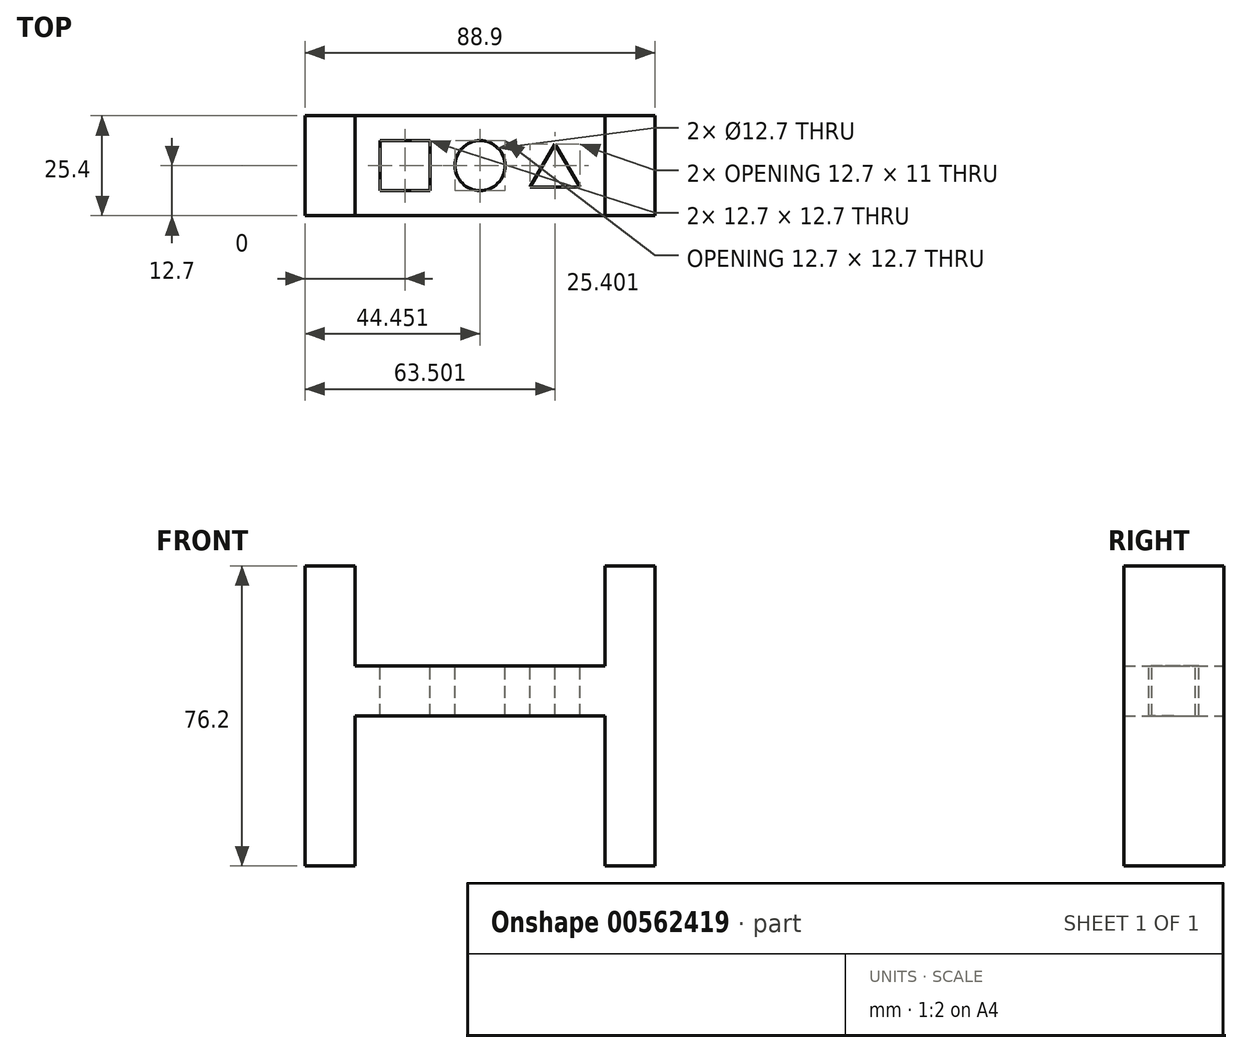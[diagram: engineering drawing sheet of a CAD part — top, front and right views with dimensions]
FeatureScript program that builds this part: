
annotation { "Feature Type Name" : "Feature", "Feature Type Description" : "" }
export const myFeature = defineFeature(function(context is Context, id is Id, definition is map)
    precondition{}
    {
        {
            var Q0;
            Q0=qCreatedBy(makeId("Front.planeOp"),FACE);
            var sketch = newSketch(context, id + "F0", { "sketchPlane" : qUnion([Q0])});
            skLineSegment(sketch, "E0", {"start": v(-59.33, 38.1) * mm, "end": v(-46.63, 38.1) * mm});
            skLineSegment(sketch, "E1", {"start": v(-46.63, 38.1) * mm, "end": v(-46.63, 12.7) * mm});
            skLineSegment(sketch, "E2", {"start": v(-46.63, 12.7) * mm, "end": v(16.87, 12.7) * mm});
            skLineSegment(sketch, "E3", {"start": v(16.87, 12.7) * mm, "end": v(16.87, 38.1) * mm});
            skLineSegment(sketch, "E4", {"start": v(16.87, 38.1) * mm, "end": v(29.57, 38.1) * mm});
            skLineSegment(sketch, "E5", {"start": v(29.57, 38.1) * mm, "end": v(29.57, -38.1) * mm});
            skLineSegment(sketch, "E6", {"start": v(29.57, -38.1) * mm, "end": v(16.87, -38.1) * mm});
            skLineSegment(sketch, "E7", {"start": v(16.87, -38.1) * mm, "end": v(16.87, 0) * mm});
            skLineSegment(sketch, "E8", {"start": v(16.87, 0) * mm, "end": v(-46.63, 0) * mm});
            skLineSegment(sketch, "E9", {"start": v(-46.63, 0) * mm, "end": v(-46.63, -38.1) * mm});
            skLineSegment(sketch, "E10", {"start": v(-46.63, -38.1) * mm, "end": v(-59.33, -38.1) * mm});
            skLineSegment(sketch, "E11", {"start": v(-59.33, -38.1) * mm, "end": v(-59.33, 38.1) * mm});
            skSolve(sketch);
        }
        {
            var Q0;
            Q0=makeQuery(id+"F0.imprint","IMPRINT",FACE,{"disambiguationData":[TD([[makeQuery(id+"F0.imprint","IMPRINT",EDGE,{"derivedFrom":sQuery(id+"F0.wireOp",EDGE,"E0")}),-1.0]])]});
            extrude(context, id + "F1", {"entities" : qUnion([Q0]), "depth" : 25.4 * mm, "offsetDistance" : 25.4 * mm});
        }
        {
            var Q0;
            Q0=makeQuery(id+"F1.opExtrude","SWEPT_FACE",FACE,{"disambiguationData":[OSD([sQuery(id+"F0.wireOp",EDGE,"E2")])]});
            var sketch = newSketch(context, id + "F2", { "sketchPlane" : qUnion([Q0])});
            skLineSegment(sketch, "E12.bottom", {"start": v(-40.28, -6.35) * mm, "end": v(-27.58, -6.35) * mm});
            skLineSegment(sketch, "E12.top", {"start": v(-40.28, -19.05) * mm, "end": v(-27.58, -19.05) * mm});
            skLineSegment(sketch, "E12.left", {"start": v(-40.28, -6.35) * mm, "end": v(-40.28, -19.05) * mm});
            skLineSegment(sketch, "E12.right", {"start": v(-27.58, -6.35) * mm, "end": v(-27.58, -19.05) * mm});
            skSolve(sketch);
        }
        {
            var Q0;
            Q0=makeQuery(id+"F2.imprint","IMPRINT",FACE,{"disambiguationData":[TD([[makeQuery(id+"F2.imprint","IMPRINT",EDGE,{"derivedFrom":sQuery(id+"F2.wireOp",EDGE,"E12.bottom")}),-1.0]])]});
            extrude(context, id + "F3", {"entities" : qUnion([Q0]), "operationType" : NewBodyOperationType.REMOVE, "oppositeDirection" : true, "depth" : 25.4 * mm, "offsetDistance" : 25.4 * mm});
        }
        {
            var Q0;
            Q0=makeQuery(id+"F1.opExtrude","SWEPT_FACE",FACE,{"disambiguationData":[OSD([sQuery(id+"F0.wireOp",EDGE,"E2")])]});
            var sketch = newSketch(context, id + "F4", { "sketchPlane" : qUnion([Q0])});
            skCircle(sketch, "E13", {"center": v(-14.88, -12.7) * mm, "radius": 6.35 * mm});
            skPoint(sketch, "E13.centerSnap0", {"position": v(-27.58, -12.7) * mm});
            skSolve(sketch);
        }
        {
            var Q0;
            Q0=makeQuery(id+"F4.imprint","IMPRINT",FACE,{"disambiguationData":[TD([[makeQuery(id+"F4.imprint","IMPRINT",EDGE,{"derivedFrom":sQuery(id+"F4.wireOp",EDGE,"E13")}),1.0]])]});
            extrude(context, id + "F5", {"entities" : qUnion([Q0]), "operationType" : NewBodyOperationType.REMOVE, "oppositeDirection" : true, "depth" : 25.4 * mm, "offsetDistance" : 25.4 * mm});
        }
        {
            var Q0;
            Q0=makeQuery(id+"F1.opExtrude","SWEPT_FACE",FACE,{"disambiguationData":[OSD([sQuery(id+"F0.wireOp",EDGE,"E2")])]});
            var sketch = newSketch(context, id + "F6", { "sketchPlane" : qUnion([Q0])});
            skLineSegment(sketch, "E14", {"start": v(-2.18, -18.2) * mm, "end": v(10.52, -18.2) * mm});
            skLineSegment(sketch, "E15", {"start": v(10.52, -18.2) * mm, "end": v(4.17, -7.2) * mm});
            skLineSegment(sketch, "E16", {"start": v(4.17, -7.2) * mm, "end": v(-2.18, -18.2) * mm});
            skSolve(sketch);
        }
        {
            var Q0;
            Q0=makeQuery(id+"F6.imprint","IMPRINT",FACE,{"disambiguationData":[TD([[makeQuery(id+"F6.imprint","IMPRINT",EDGE,{"derivedFrom":sQuery(id+"F6.wireOp",EDGE,"E14")}),1.0]])]});
            extrude(context, id + "F7", {"entities" : qUnion([Q0]), "operationType" : NewBodyOperationType.REMOVE, "oppositeDirection" : true, "depth" : 25.4 * mm, "offsetDistance" : 25.4 * mm});
        }
    });
